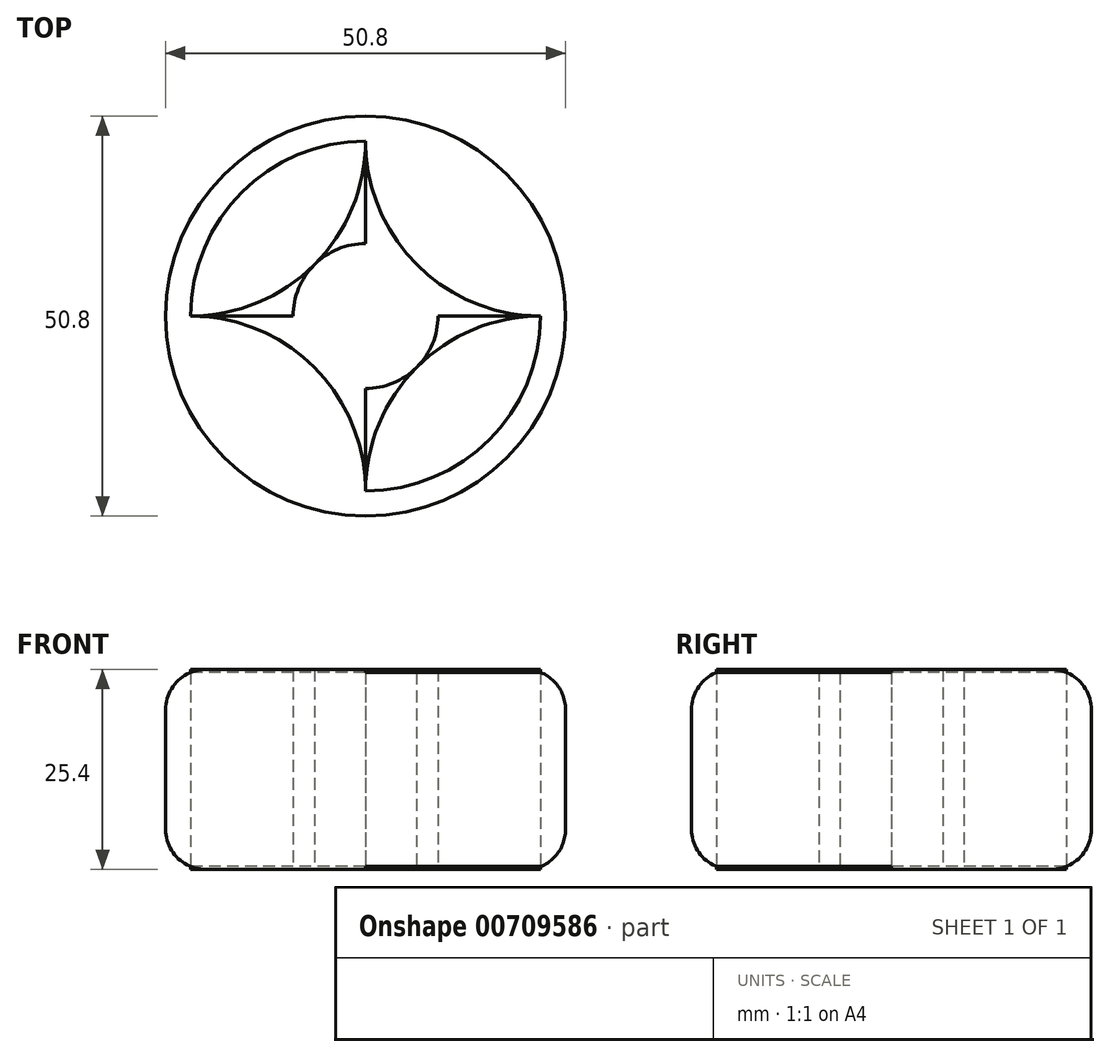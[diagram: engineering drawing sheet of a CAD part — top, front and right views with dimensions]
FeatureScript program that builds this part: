
annotation { "Feature Type Name" : "Feature", "Feature Type Description" : "" }
export const myFeature = defineFeature(function(context is Context, id is Id, definition is map)
    precondition{}
    {
        {
            var Q0;
            Q0=qCreatedBy(makeId("Top.planeOp"),FACE);
            var sketch = newSketch(context, id + "F0", { "sketchPlane" : qUnion([Q0])});
            skCircle(sketch, "E0", {"center": v(0, 0) * mm, "radius": 25.4 * mm});
            skCircle(sketch, "E1", {"center": v(0, 0) * mm, "radius": 1.59 * mm});
            skCircle(sketch, "E2", {"center": v(0, 0) * mm, "radius": 22.23 * mm});
            skLineSegment(sketch, "E3", {"start": v(0, 0) * mm, "end": v(22.23, 0) * mm, "construction": true});
            skLineSegment(sketch, "E4", {"start": v(0, 0) * mm, "end": v(0, 22.23) * mm, "construction": true});
            skLineSegment(sketch, "E5", {"start": v(0, 22.22) * mm, "end": v(22.22, 0) * mm, "construction": true});
            skLineSegment(sketch, "E6", {"start": v(0, 0) * mm, "end": v(15.72, 15.72) * mm, "construction": true});
            skArc(sketch, "E7", {"start": v(0, 22.22) * mm, "mid": v(6.5, 6.5) * mm, "end": v(22.23, 0) * mm});
            skArc(sketch, "E8.MirrorCS", {"start": v(0, 22.22) * mm, "mid": v(-6.5, 6.5) * mm, "end": v(-22.23, 0) * mm});
            skLineSegment(sketch, "E9", {"start": v(-22.23, 0) * mm, "end": v(22.23, 0) * mm});
            skLineSegment(sketch, "E10", {"start": v(0, 22.23) * mm, "end": v(0, -22.23) * mm});
            skArc(sketch, "E11.MirrorCS", {"start": v(0, -22.22) * mm, "mid": v(-6.5, -6.5) * mm, "end": v(-22.23, 0) * mm});
            skArc(sketch, "E12.MirrorCS", {"start": v(0, -22.22) * mm, "mid": v(6.5, -6.5) * mm, "end": v(22.23, 0) * mm});
            skCircle(sketch, "E13", {"center": v(0, 0) * mm, "radius": 9.2 * mm});
            skSolve(sketch);
        }
        {
            var Q0;
            Q0=makeQuery(id+"F0.imprint","IMPRINT",FACE,{"disambiguationData":[TD([[makeQuery(id+"F0.imprint","IMPRINT",EDGE,{"derivedFrom":sQuery(id+"F0.wireOp",EDGE,"E0")}),1.0]])]});
            var Q1;
            {var subQ0=sQuery(id+"F0.wireOp",EDGE,"E8.MirrorCS");Q1=makeQuery(id+"F0.imprint","IMPRINT",FACE,{"disambiguationData":[TD([[makeQuery(id+"F0.imprint","IMPRINT",EDGE,{"derivedFrom":subQ0}),-1.0]])]});}
            var Q2;
            {var subQ0=sQuery(id+"F0.wireOp",EDGE,"E7");Q2=makeQuery(id+"F0.imprint","IMPRINT",FACE,{"disambiguationData":[TD([[makeQuery(id+"F0.imprint","IMPRINT",EDGE,{"derivedFrom":subQ0}),1.0]])]});}
            var Q3;
            {var subQ0=sQuery(id+"F0.wireOp",EDGE,"E11.MirrorCS");Q3=makeQuery(id+"F0.imprint","IMPRINT",FACE,{"disambiguationData":[TD([[makeQuery(id+"F0.imprint","IMPRINT",EDGE,{"derivedFrom":subQ0}),1.0]])]});}
            var Q4;
            {var subQ0=sQuery(id+"F0.wireOp",EDGE,"E12.MirrorCS");Q4=makeQuery(id+"F0.imprint","IMPRINT",FACE,{"disambiguationData":[TD([[makeQuery(id+"F0.imprint","IMPRINT",EDGE,{"derivedFrom":subQ0}),-1.0]])]});}
            extrude(context, id + "F1", {"entities" : qUnion([Q0, Q1, Q2, Q3, Q4]), "depth" : 25.4 * mm, "offsetDistance" : 25.4 * mm});
        }
        {
            var Q0;
            Q0=makeQuery(id+"F1.opExtrude","CAP_EDGE",EDGE,{"disambiguationData":[OSD([sQuery(id+"F0.wireOp",EDGE,"E0")])],"isStart":false});
            var Q1;
            Q1=makeQuery(id+"F1.opExtrude","CAP_EDGE",EDGE,{"disambiguationData":[OSD([sQuery(id+"F0.wireOp",EDGE,"E0")])],"isStart":true});
            fillet(context, id + "F2", {"entities" : qUnion([Q0, Q1]), "tangentPropagation" : true, "radius" : 5.08 * mm, "defaultsChanged" : false, "vertexSettings" : [], "allowEdgeOverflow" : false});
        }
    });
